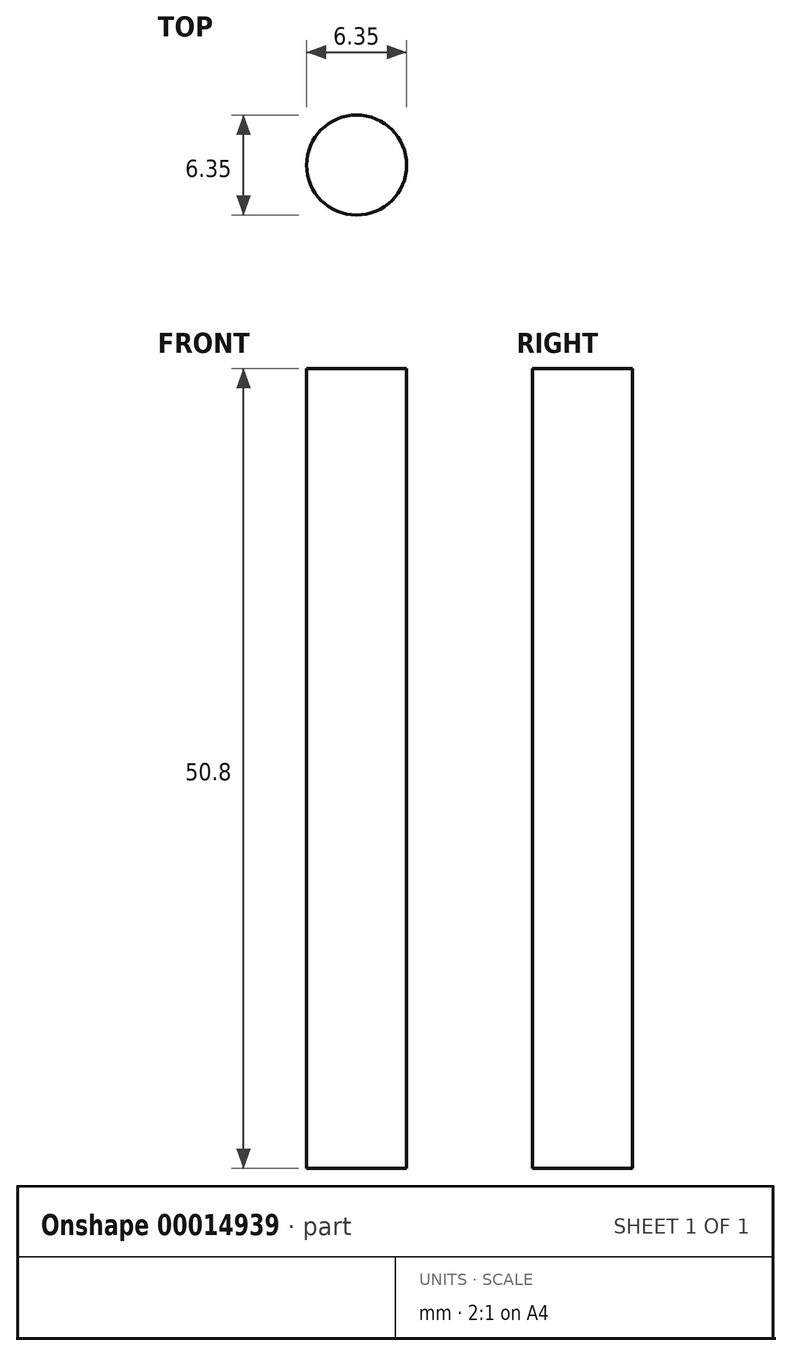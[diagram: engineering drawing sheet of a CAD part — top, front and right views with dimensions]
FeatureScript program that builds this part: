
annotation { "Feature Type Name" : "Feature", "Feature Type Description" : "" }
export const myFeature = defineFeature(function(context is Context, id is Id, definition is map)
    precondition{}
    {
        {
            var Q0;
            Q0=qCreatedBy(makeId("Top.planeOp"),FACE);
            var sketch = newSketch(context, id + "F0", { "sketchPlane" : qUnion([Q0])});
            skCircle(sketch, "E0", {"center": v(-33.68, 24.41) * mm, "radius": 3.18 * mm});
            skSolve(sketch);
        }
        {
            var Q0;
            Q0=makeQuery(id+"F0.imprint","IMPRINT",FACE,{"disambiguationData":[TD([[makeQuery(id+"F0.imprint","IMPRINT",EDGE,{"derivedFrom":sQuery(id+"F0.wireOp",EDGE,"E0")}),1.0]])]});
            extrude(context, id + "F1", {"entities" : qUnion([Q0]), "depth" : 50.8 * mm});
        }
    });
